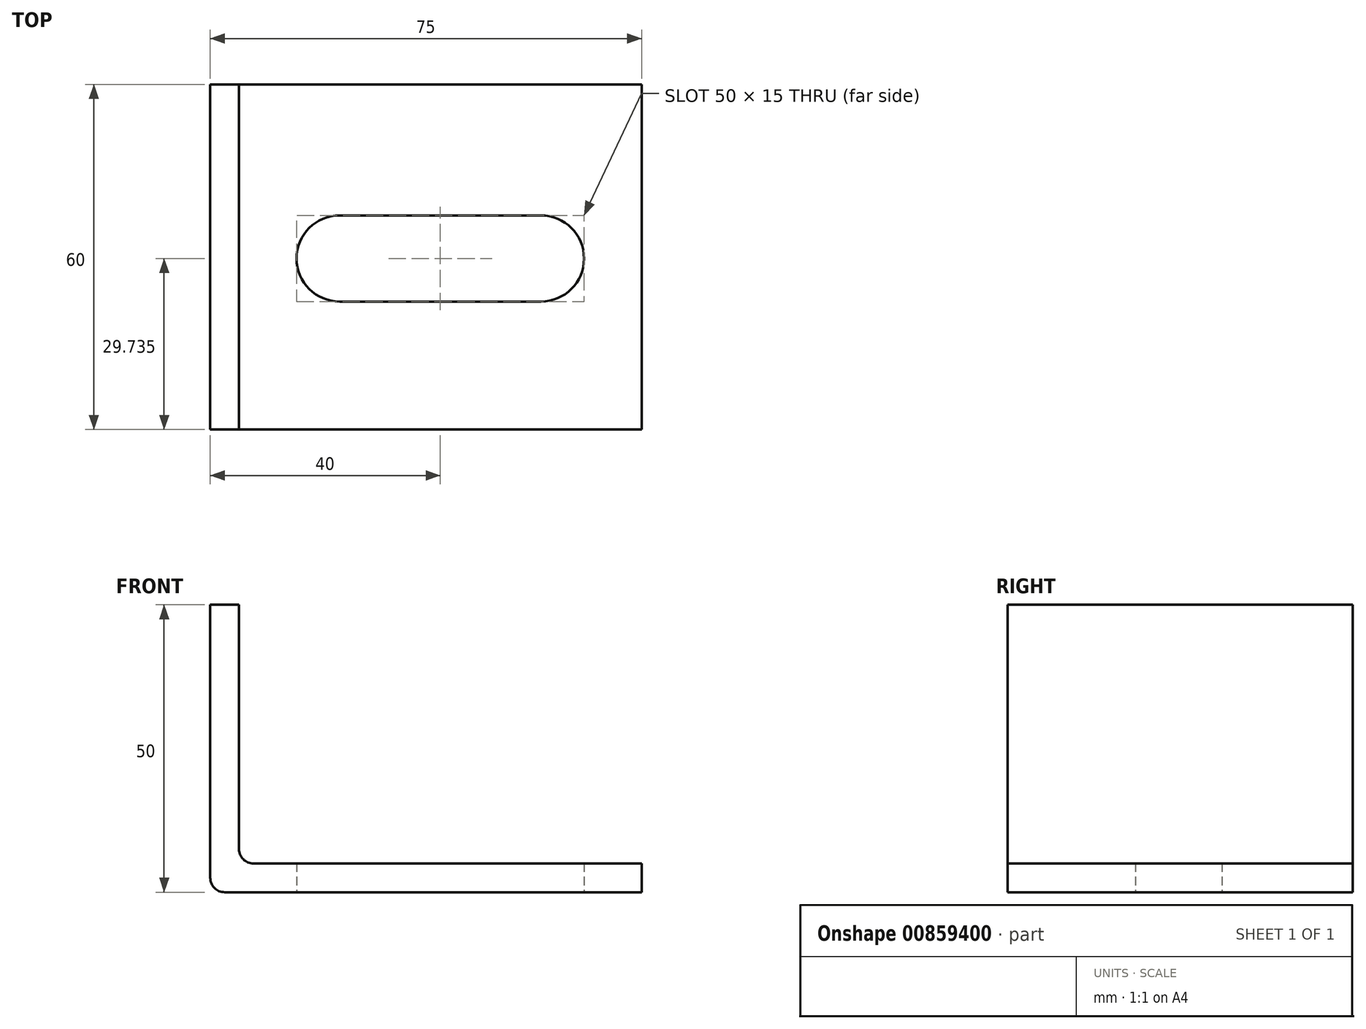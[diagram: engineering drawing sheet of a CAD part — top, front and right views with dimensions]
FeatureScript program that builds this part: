
annotation { "Feature Type Name" : "Feature", "Feature Type Description" : "" }
export const myFeature = defineFeature(function(context is Context, id is Id, definition is map)
    precondition{}
    {
        {
            var Q0;
            Q0=qCreatedBy(makeId("Front.planeOp"),FACE);
            var sketch = newSketch(context, id + "F0", { "sketchPlane" : qUnion([Q0])});
            skLineSegment(sketch, "E0", {"start": v(0, 50) * mm, "end": v(0, 2.5) * mm});
            skLineSegment(sketch, "E1", {"start": v(2.5, 0) * mm, "end": v(75, 0) * mm});
            skLineSegment(sketch, "E2.0", {"start": v(7.5, 5) * mm, "end": v(75, 5) * mm});
            skLineSegment(sketch, "E2.1", {"start": v(5, 50) * mm, "end": v(5, 7.5) * mm});
            skLineSegment(sketch, "E3", {"start": v(0, 50) * mm, "end": v(5, 50) * mm});
            skLineSegment(sketch, "E4", {"start": v(75, 5) * mm, "end": v(75, 0) * mm});
            skPoint(sketch, "E5.visualSharp", {"position": v(0, 0) * mm});
            skArc(sketch, "E5.filletArc", {"start": v(0, 2.5) * mm, "mid": v(0.73, 0.73) * mm, "end": v(2.5, 0) * mm});
            skPoint(sketch, "E6.visualSharp", {"position": v(5, 5) * mm});
            skArc(sketch, "E6.filletArc", {"start": v(5, 7.5) * mm, "mid": v(5.73, 5.73) * mm, "end": v(7.5, 5) * mm});
            skSolve(sketch);
        }
        {
            var Q0;
            Q0 = qSketchRegion(id + "F0", true);
            extrude(context, id + "F1", {"entities" : qUnion([Q0]), "oppositeDirection" : true, "depth" : 60 * mm, "offsetDistance" : 25 * mm});
        }
        {
            var Q0;
            Q0=makeQuery(id+"F1.opExtrude","SWEPT_FACE",FACE,{"disambiguationData":[OSD([sQuery(id+"F0.wireOp",EDGE,"E1")])]});
            var sketch = newSketch(context, id + "F2", { "sketchPlane" : qUnion([Q0])});
            skLineSegment(sketch, "E7.bottom", {"start": v(22.5, -22.24) * mm, "end": v(57.5, -22.24) * mm});
            skLineSegment(sketch, "E7.top", {"start": v(22.5, -37.24) * mm, "end": v(57.5, -37.24) * mm});
            skLineSegment(sketch, "E7.left", {"start": v(22.5, -22.24) * mm, "end": v(22.5, -37.24) * mm});
            skLineSegment(sketch, "E7.right", {"start": v(57.5, -22.24) * mm, "end": v(57.5, -37.24) * mm});
            skArc(sketch, "E8", {"start": v(57.5, -22.24) * mm, "mid": v(65, -29.74) * mm, "end": v(57.5, -37.24) * mm});
            skArc(sketch, "E9", {"start": v(22.5, -22.24) * mm, "mid": v(15, -29.74) * mm, "end": v(22.5, -37.24) * mm});
            skSolve(sketch);
        }
        {
            var Q0;
            Q0 = qSketchRegion(id + "F2", true);
            extrude(context, id + "F3", {"entities" : qUnion([Q0]), "operationType" : NewBodyOperationType.REMOVE, "endBound" : BoundingType.THROUGH_ALL, "oppositeDirection" : true, "depth" : 25 * mm, "offsetDistance" : 25 * mm});
        }
    });
